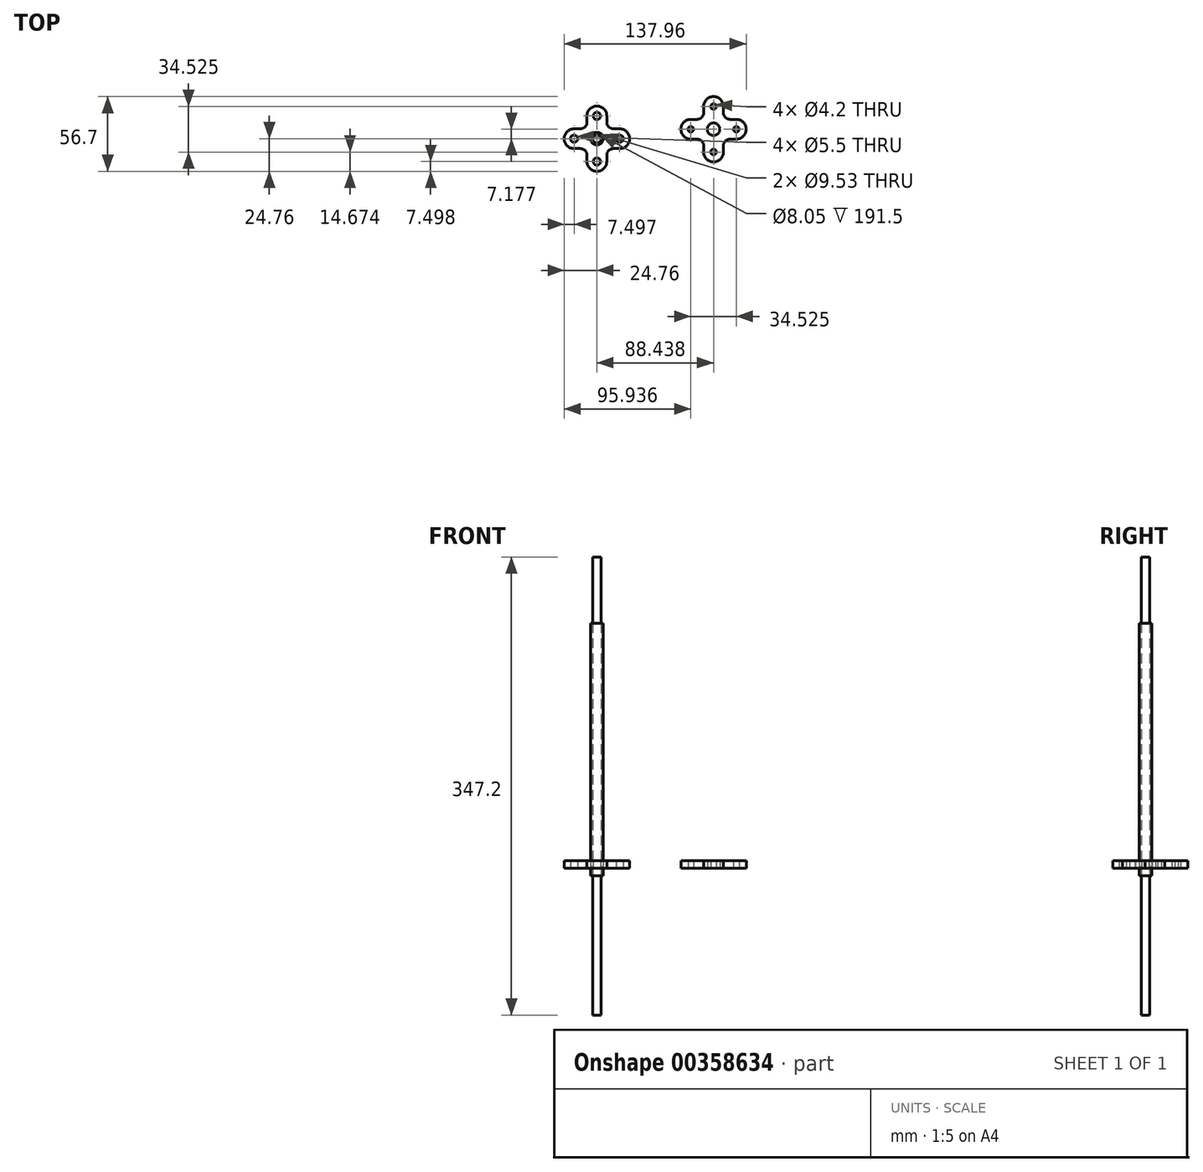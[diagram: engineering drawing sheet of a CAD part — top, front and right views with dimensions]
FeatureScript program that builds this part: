
annotation { "Feature Type Name" : "Feature", "Feature Type Description" : "" }
export const myFeature = defineFeature(function(context is Context, id is Id, definition is map)
    precondition{}
    {
        {
            var Q0;
            Q0=qCreatedBy(makeId("Top.planeOp"),FACE);
            var sketch = newSketch(context, id + "F0", { "sketchPlane" : qUnion([Q0])});
            skCircle(sketch, "E0", {"center": v(0, 0) * mm, "radius": 3.17 * mm});
            skSolve(sketch);
        }
        {
            var Q0;
            Q0=makeQuery(id+"F0.imprint","IMPRINT",FACE,{"disambiguationData":[TD([[makeQuery(id+"F0.imprint","IMPRINT",EDGE,{"derivedFrom":sQuery(id+"F0.wireOp",EDGE,"E0")}),1.0]])]});
            extrude(context, id + "F1", {"entities" : qUnion([Q0]), "depth" : 235.8 * mm, "hasSecondDirection" : true, "secondDirectionOppositeDirection" : true, "secondDirectionDepth" : (80 + 31.4) * mm, "offsetDistance" : 25 * mm});
        }
        {
            var Q0;
            Q0=qCreatedBy(makeId("Top.planeOp"),FACE);
            var sketch = newSketch(context, id + "F2", { "sketchPlane" : qUnion([Q0])});
            skCircle(sketch, "E1", {"center": v(0, 0) * mm, "radius": 4.03 * mm});
            skCircle(sketch, "E2", {"center": v(0, 0) * mm, "radius": 4.76 * mm});
            skSolve(sketch);
        }
        {
            var Q0;
            Q0=makeQuery(id+"F2.imprint","IMPRINT",FACE,{"disambiguationData":[TD([[makeQuery(id+"F2.imprint","IMPRINT",EDGE,{"derivedFrom":sQuery(id+"F2.wireOp",EDGE,"E1")}),-1.0]])]});
            extrude(context, id + "F3", {"entities" : qUnion([Q0]), "depth" : 185.8 * mm, "hasSecondDirection" : true, "secondDirectionOppositeDirection" : true, "secondDirectionDepth" : 5.7 * mm, "offsetDistance" : 25 * mm});
        }
        {
            var Q0;
            Q0=qCreatedBy(makeId("Top.planeOp"),FACE);
            var sketch = newSketch(context, id + "F4", { "sketchPlane" : qUnion([Q0])});
            skCircle(sketch, "E3", {"center": v(0, 0) * mm, "radius": 4.76 * mm});
            skLineSegment(sketch, "E4", {"start": v(0, 27.76) * mm, "end": v(0, -29.66) * mm, "construction": true});
            skLineSegment(sketch, "E5", {"start": v(-30.82, 0) * mm, "end": v(28.88, 0) * mm, "construction": true});
            skLineSegment(sketch, "E6", {"start": v(-7.5, 17.26) * mm, "end": v(-7.5, 12.5) * mm});
            skLineSegment(sketch, "E7", {"start": v(7.5, 12.5) * mm, "end": v(7.5, 17.26) * mm});
            skLineSegment(sketch, "E8", {"start": v(-24.76, 0) * mm, "end": v(-24.76, -0.04) * mm});
            skLineSegment(sketch, "E9", {"start": v(12.5, 7.5) * mm, "end": v(17.26, 7.5) * mm});
            skArc(sketch, "E10", {"start": v(7.5, 17.26) * mm, "mid": v(0, 24.76) * mm, "end": v(-7.5, 17.26) * mm});
            skArc(sketch, "E11", {"start": v(-17.26, 7.5) * mm, "mid": v(-24.76, 0) * mm, "end": v(-17.26, -7.5) * mm});
            skArc(sketch, "E12", {"start": v(17.26, -7.5) * mm, "mid": v(24.76, 0) * mm, "end": v(17.26, 7.5) * mm});
            skArc(sketch, "E13", {"start": v(-7.5, -17.26) * mm, "mid": v(0, -24.76) * mm, "end": v(7.5, -17.26) * mm});
            skArc(sketch, "E14.filletArc", {"start": v(7.5, 12.5) * mm, "mid": v(8.96, 8.96) * mm, "end": v(12.5, 7.5) * mm});
            skLineSegment(sketch, "E15", {"start": v(7.5, -17.26) * mm, "end": v(7.5, -12.5) * mm});
            skLineSegment(sketch, "E16.trimOffspring", {"start": v(12.5, -7.5) * mm, "end": v(17.26, -7.5) * mm});
            skLineSegment(sketch, "E17", {"start": v(-17.26, -7.5) * mm, "end": v(-12.5, -7.5) * mm});
            skLineSegment(sketch, "E18", {"start": v(-17.26, 7.5) * mm, "end": v(-12.5, 7.5) * mm});
            skLineSegment(sketch, "E19.trimOffspring", {"start": v(-7.5, -12.5) * mm, "end": v(-7.5, -17.26) * mm});
            skArc(sketch, "E20.filletArc", {"start": v(-12.5, 7.5) * mm, "mid": v(-8.96, 8.96) * mm, "end": v(-7.5, 12.5) * mm});
            skArc(sketch, "E21.filletArc", {"start": v(-7.5, -12.5) * mm, "mid": v(-8.96, -8.96) * mm, "end": v(-12.5, -7.5) * mm});
            skArc(sketch, "E22.filletArc", {"start": v(12.5, -7.5) * mm, "mid": v(8.96, -8.96) * mm, "end": v(7.5, -12.5) * mm});
            skCircle(sketch, "E23", {"center": v(0, 17.26) * mm, "radius": 2.75 * mm});
            skCircle(sketch, "E24", {"center": v(-17.26, 0) * mm, "radius": 2.75 * mm});
            skCircle(sketch, "E25", {"center": v(0, -17.26) * mm, "radius": 2.75 * mm});
            skCircle(sketch, "E26", {"center": v(17.26, 0) * mm, "radius": 2.75 * mm});
            skSolve(sketch);
        }
        {
            var Q0;
            Q0=qCreatedBy(makeId("Top.planeOp"),FACE);
            var sketch = newSketch(context, id + "F5", { "sketchPlane" : qUnion([Q0])});
            skCircle(sketch, "E27", {"center": v(88.44, 7.18) * mm, "radius": 4.76 * mm});
            skLineSegment(sketch, "E28", {"start": v(88.44, 34.94) * mm, "end": v(88.44, -22.49) * mm, "construction": true});
            skLineSegment(sketch, "E29", {"start": v(57.62, 7.18) * mm, "end": v(117.32, 7.18) * mm, "construction": true});
            skLineSegment(sketch, "E30", {"start": v(80.94, 24.44) * mm, "end": v(80.94, 19.68) * mm});
            skLineSegment(sketch, "E31", {"start": v(95.94, 19.68) * mm, "end": v(95.94, 24.44) * mm});
            skLineSegment(sketch, "E32", {"start": v(63.68, 7.18) * mm, "end": v(63.68, 7.14) * mm});
            skLineSegment(sketch, "E33", {"start": v(100.94, 14.68) * mm, "end": v(105.7, 14.68) * mm});
            skArc(sketch, "E34", {"start": v(95.94, 24.44) * mm, "mid": v(88.44, 31.94) * mm, "end": v(80.94, 24.44) * mm});
            skArc(sketch, "E35", {"start": v(71.18, 14.68) * mm, "mid": v(63.68, 7.18) * mm, "end": v(71.18, -0.32) * mm});
            skArc(sketch, "E36", {"start": v(105.7, -0.32) * mm, "mid": v(113.2, 7.18) * mm, "end": v(105.7, 14.68) * mm});
            skArc(sketch, "E37", {"start": v(80.94, -10.09) * mm, "mid": v(88.44, -17.59) * mm, "end": v(95.94, -10.09) * mm});
            skArc(sketch, "E38.filletArc", {"start": v(95.94, 19.68) * mm, "mid": v(97.4, 16.14) * mm, "end": v(100.94, 14.68) * mm});
            skLineSegment(sketch, "E39", {"start": v(95.94, -10.09) * mm, "end": v(95.94, -5.32) * mm});
            skLineSegment(sketch, "E40.trimOffspring", {"start": v(100.94, -0.32) * mm, "end": v(105.7, -0.32) * mm});
            skLineSegment(sketch, "E41", {"start": v(71.18, -0.32) * mm, "end": v(75.94, -0.32) * mm});
            skLineSegment(sketch, "E42", {"start": v(71.18, 14.68) * mm, "end": v(75.94, 14.68) * mm});
            skLineSegment(sketch, "E43.trimOffspring", {"start": v(80.94, -5.32) * mm, "end": v(80.94, -10.09) * mm});
            skArc(sketch, "E44.filletArc", {"start": v(75.94, 14.68) * mm, "mid": v(79.47, 16.14) * mm, "end": v(80.94, 19.68) * mm});
            skArc(sketch, "E45.filletArc", {"start": v(80.94, -5.32) * mm, "mid": v(79.47, -1.79) * mm, "end": v(75.94, -0.32) * mm});
            skArc(sketch, "E46.filletArc", {"start": v(100.94, -0.32) * mm, "mid": v(97.4, -1.79) * mm, "end": v(95.94, -5.32) * mm});
            skCircle(sketch, "E47", {"center": v(88.44, 24.44) * mm, "radius": 2.1 * mm});
            skCircle(sketch, "E48", {"center": v(71.18, 7.18) * mm, "radius": 2.1 * mm});
            skCircle(sketch, "E49", {"center": v(88.44, -10.09) * mm, "radius": 2.1 * mm});
            skCircle(sketch, "E50", {"center": v(105.7, 7.18) * mm, "radius": 2.1 * mm});
            skSolve(sketch);
        }
        {
            var Q0;
            Q0=makeQuery(id+"F4.imprint","IMPRINT",FACE,{"disambiguationData":[TD([[makeQuery(id+"F4.imprint","IMPRINT",EDGE,{"derivedFrom":sQuery(id+"F4.wireOp",EDGE,"E3")}),-1.0]])]});
            extrude(context, id + "F6", {"entities" : qUnion([Q0]), "depth" : 5.6 * mm, "offsetDistance" : 25 * mm});
        }
        {
            var Q0;
            Q0=makeQuery(id+"F5.imprint","IMPRINT",FACE,{"disambiguationData":[TD([[makeQuery(id+"F5.imprint","IMPRINT",EDGE,{"derivedFrom":sQuery(id+"F5.wireOp",EDGE,"E27")}),-1.0]])]});
            extrude(context, id + "F7", {"entities" : qUnion([Q0]), "depth" : 5.6 * mm, "offsetDistance" : 25 * mm});
        }
    });
